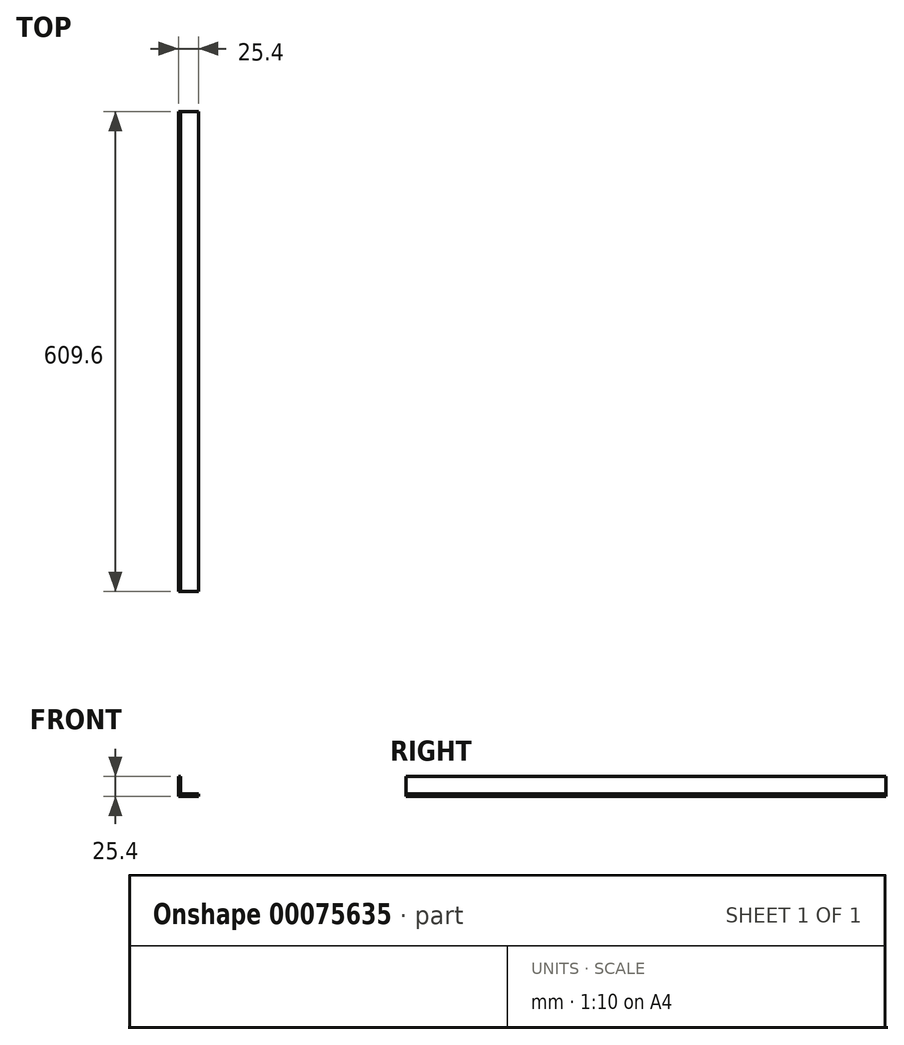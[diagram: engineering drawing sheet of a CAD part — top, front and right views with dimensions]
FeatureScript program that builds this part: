
annotation { "Feature Type Name" : "Feature", "Feature Type Description" : "" }
export const myFeature = defineFeature(function(context is Context, id is Id, definition is map)
    precondition{}
    {
        {
            var Q0;
            Q0=qCreatedBy(makeId("Front.planeOp"),FACE);
            var sketch = newSketch(context, id + "F0", { "sketchPlane" : qUnion([Q0])});
            skLineSegment(sketch, "E0", {"start": v(0, 0) * mm, "end": v(0, 25.4) * mm});
            skLineSegment(sketch, "E1", {"start": v(0, 25.4) * mm, "end": v(3.17, 25.4) * mm});
            skLineSegment(sketch, "E2", {"start": v(3.17, 25.4) * mm, "end": v(3.18, 3.17) * mm});
            skLineSegment(sketch, "E3", {"start": v(3.18, 3.17) * mm, "end": v(25.4, 3.18) * mm});
            skLineSegment(sketch, "E4", {"start": v(25.4, 3.18) * mm, "end": v(25.4, 0) * mm});
            skLineSegment(sketch, "E5", {"start": v(25.4, 0) * mm, "end": v(0, 0) * mm});
            skSolve(sketch);
        }
        {
            var Q0;
            Q0 = qSketchRegion(id + "F0", true);
            extrude(context, id + "F1", {"entities" : qUnion([Q0]), "depth" : 609.6 * mm});
        }
    });
